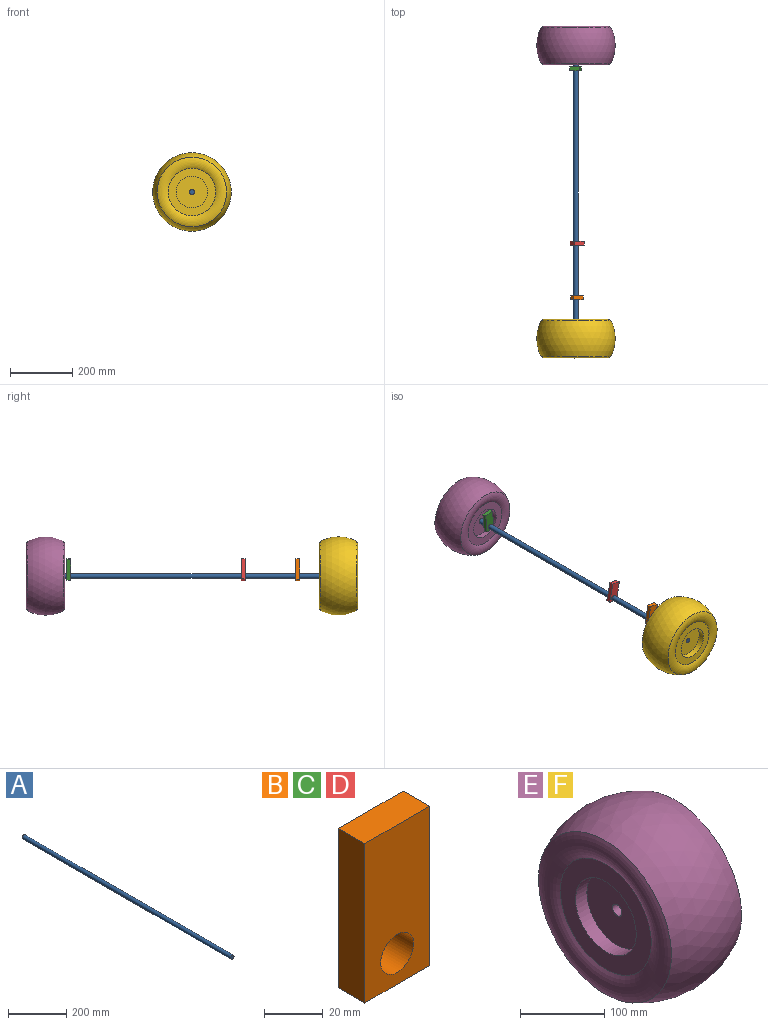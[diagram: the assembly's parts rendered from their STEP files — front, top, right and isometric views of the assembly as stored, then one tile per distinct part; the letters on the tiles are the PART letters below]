
ASSEMBLY  parts=6 mates=5
PART A: 3 faces, bbox 15.9x1016x15.9 mm
  f0: cylinder r=7.94mm len=1016mm, axis (0,1,0), area 50670.7mm2, adj f1,f2
  f1: plane 15.88x15.88mm, normal (0,-1,0), area 197.9mm2, adj f0
  f2: plane 15.88x15.88mm, normal (0,1,0), area 197.9mm2, adj f0
PART B: 7 faces, bbox 31.3x12.7x66.5 mm
  f0: plane 31.29x12.7mm, normal (0,0,-1), area 397.4mm2, adj f1,f3,f4,f5
  f1: plane 66.5x12.7mm, normal (1,0,0), area 844.5mm2, adj f0,f2,f4,f5
  f2: plane 31.29x12.7mm, normal (0,0,1), area 397.4mm2, adj f1,f3,f4,f5
  f3: plane 66.5x12.7mm, normal (-1,0,0), area 844.5mm2, adj f0,f2,f4,f5
  f4: plane 66.5x31.29mm, normal (0,-1,0), area 1883mm2, adj f0,f1,f2,f3,f6
  f5: plane 66.5x31.29mm, normal (0,1,0), area 1883mm2, adj f0,f1,f2,f3,f6
  f6: cylinder r=7.94mm len=15.88mm, axis (0,-1,0), area 633.4mm2, adj f4,f5
PART C: same geometry as B
PART D: same geometry as B
PART E: 10 faces, bbox 124.5x264.8x264.8 mm
  f0: plane 152.4x152.4mm, normal (-1,0,0), area 10134.1mm2, adj f1,f8
  f1: cylinder r=50.8mm len=101.6mm, axis (-1,0,0), area 6080.5mm2, adj f0,f2
  f2: plane 101.6x101.6mm, normal (-1,0,0), area 7909.4mm2, adj f1,f9
  f3: plane 101.6x101.6mm, normal (1,0,0), area 7909.4mm2, adj f4,f9
  f4: cylinder r=50.8mm len=101.6mm, axis (-1,0,0), area 6080.5mm2, adj f3,f5
  f5: plane 152.4x152.4mm, normal (1,0,0), area 10134.1mm2, adj f4,f6
  f6: torus R=95.25mm, axis (-1,0,0), area 21499mm2, adj f5,f7
  f7: sphere r=125.85mm, area 92829.9mm2, adj f6,f8
  f8: torus R=95.25mm, axis (-1,0,0), area 21499mm2, adj f0,f7
  f9: cylinder r=7.94mm len=76.2mm, axis (1,0,0), area 3800.3mm2, adj f2,f3
PART F: same geometry as E
PLACE A t=(18.7,170.07,-66.38)mm fixed
PLACE B rot(axis=(0,1,0),8.4deg) t=(21.67,-670.77,-46.28)mm
PLACE C rot(axis=(0,-1,0),5.3deg) t=(16.82,63.72,-46.15)mm
PLACE D rot(axis=(0,1,0),12.2deg) t=(23,-495.83,-46.52)mm
PLACE E rot(axis=(0.58,0.58,0.58),120deg) t=(18.7,131.97,-66.38)mm
PLACE F rot(axis=(-0.58,0.58,-0.58),120deg) t=(18.7,-807.83,-66.38)mm
MATE cylindrical C.f6 <-> A.f0  axis (0,-1,0) through (18.7,51.02,-66.38)mm
MATE cylindrical B.f6 <-> A.f0  axis (0,-1,0) through (18.7,-683.47,-66.38)mm
MATE cylindrical D.f6 <-> A.f0  axis (0,-1,0) through (18.7,-508.53,-66.38)mm
MATE revolute E.f1 <-> A.f0  axis (0,1,0) through (18.7,170.07,-66.38)mm
MATE revolute F.f1 <-> A.f0  axis (0,-1,0) through (18.7,-845.93,-66.38)mm
